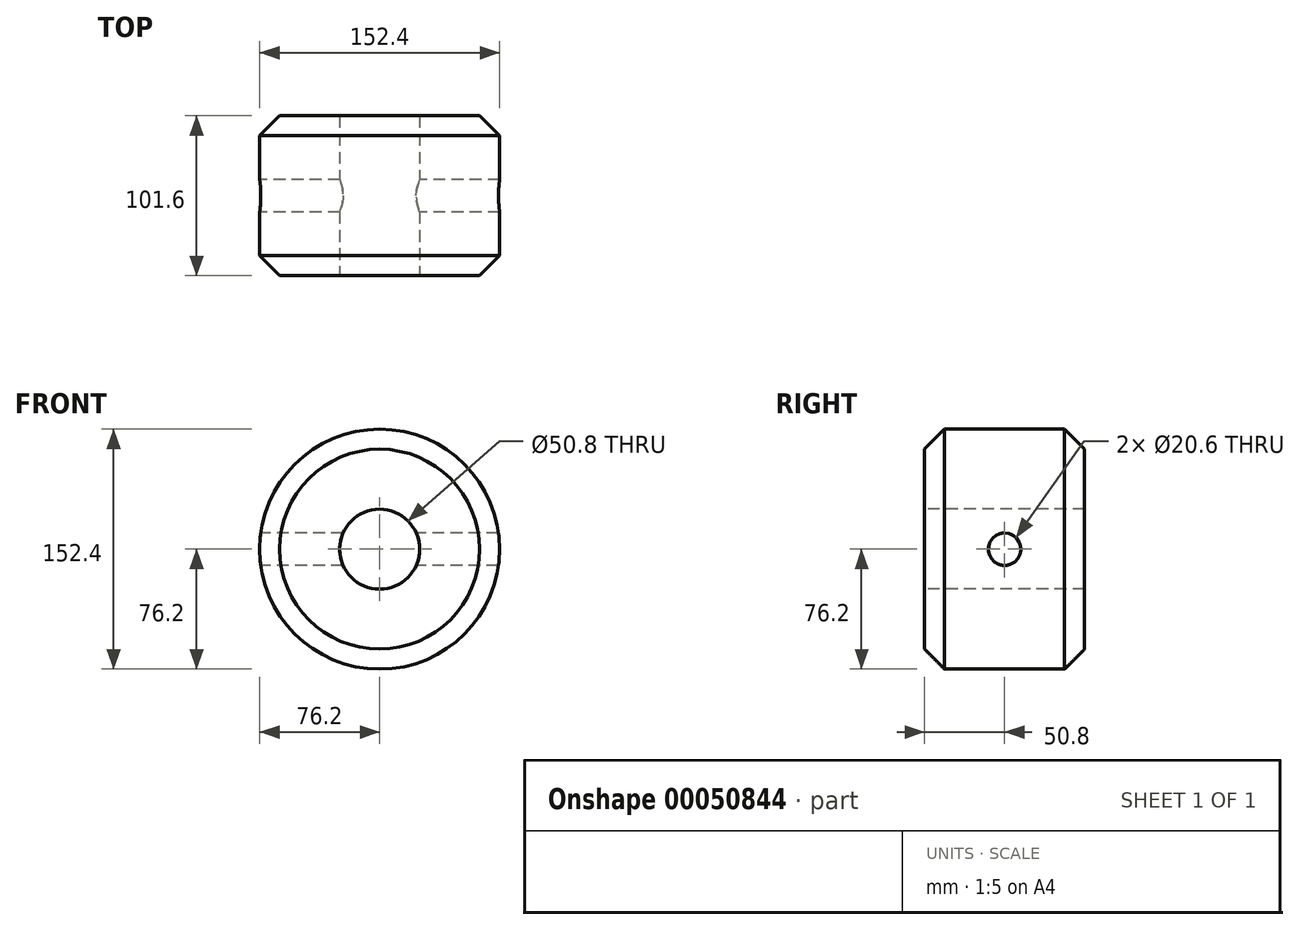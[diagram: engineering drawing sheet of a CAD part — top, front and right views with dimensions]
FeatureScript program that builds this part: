
annotation { "Feature Type Name" : "Feature", "Feature Type Description" : "" }
export const myFeature = defineFeature(function(context is Context, id is Id, definition is map)
    precondition{}
    {
        {
            var Q0;
            Q0=qCreatedBy(makeId("Front.planeOp"),FACE);
            var sketch = newSketch(context, id + "F0", { "sketchPlane" : qUnion([Q0])});
            skCircle(sketch, "E0", {"center": v(0, 0) * mm, "radius": 76.2 * mm});
            skSolve(sketch);
        }
        {
            var Q0;
            Q0 = qSketchRegion(id + "F0", true);
            extrude(context, id + "F1", {"entities" : qUnion([Q0]), "depth" : 50.8 * mm, "hasSecondDirection" : true, "secondDirectionOppositeDirection" : true, "secondDirectionDepth" : 50.8 * mm});
        }
        {
            var Q0;
            Q0=makeQuery(id+"F1.opExtrude","CAP_FACE",FACE,{"disambiguationData":[OSD([sQuery(id+"F0.wireOp",EDGE,"E0")])],"isStart":false});
            var sketch = newSketch(context, id + "F2", { "sketchPlane" : qUnion([Q0])});
            skCircle(sketch, "E1", {"center": v(0, 0) * mm, "radius": 25.4 * mm});
            skSolve(sketch);
        }
        {
            var Q0;
            Q0 = qSketchRegion(id + "F2", true);
            extrude(context, id + "F3", {"entities" : qUnion([Q0]), "operationType" : NewBodyOperationType.REMOVE, "endBound" : BoundingType.THROUGH_ALL, "oppositeDirection" : true, "depth" : 25.4 * mm});
        }
        {
            var Q0;
            Q0=makeQuery(id+"F1.opExtrude","CAP_EDGE",EDGE,{"disambiguationData":[OSD([sQuery(id+"F0.wireOp",EDGE,"E0")])],"isStart":false});
            var Q1;
            Q1=makeQuery(id+"F1.opExtrude","CAP_EDGE",EDGE,{"disambiguationData":[OSD([sQuery(id+"F0.wireOp",EDGE,"E0")])],"isStart":true});
            chamfer(context, id + "F4", {"entities" : qUnion([Q0, Q1]), "width" : 12.7 * mm, "tangentPropagation" : true});
        }
        {
            var Q0;
            Q0=qCreatedBy(makeId("Right.planeOp"),FACE);
            var sketch = newSketch(context, id + "F5", { "sketchPlane" : qUnion([Q0])});
            skCircle(sketch, "E2", {"center": v(0, 0) * mm, "radius": 10.3 * mm});
            skSolve(sketch);
        }
        {
            var Q0;
            Q0=makeQuery(id+"F5.imprint","IMPRINT",FACE,{"disambiguationData":[TD([[makeQuery(id+"F5.imprint","IMPRINT",EDGE,{"derivedFrom":sQuery(id+"F5.wireOp",EDGE,"E2")}),1.0]])]});
            extrude(context, id + "F6", {"entities" : qUnion([Q0]), "operationType" : NewBodyOperationType.REMOVE, "endBound" : BoundingType.SYMMETRIC, "depth" : 304.8 * mm});
        }
    });
